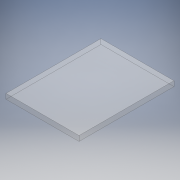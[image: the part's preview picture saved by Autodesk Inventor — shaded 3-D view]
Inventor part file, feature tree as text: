
AUTODESK INVENTOR PART (.ipt)
format: ipt  version: 2017 (Build 210142000, 142)  size: 93,696 bytes
history: native  units: mm
features: extrude x1, sketch x1
ambient origin geometry x8: Origin, YZ Plane, XZ Plane, XY Plane, X Axis, Y Axis, Z Axis, Center Point
bodies: Solid1 (feature_tree)
feature tree (2):
  extrude  "Extrusion1"  Depth=130.0mm
  sketch  "Sketch1"  dims[d0=100.0mm d1=130.0mm d2=7.0mm d3=0.0mm]
